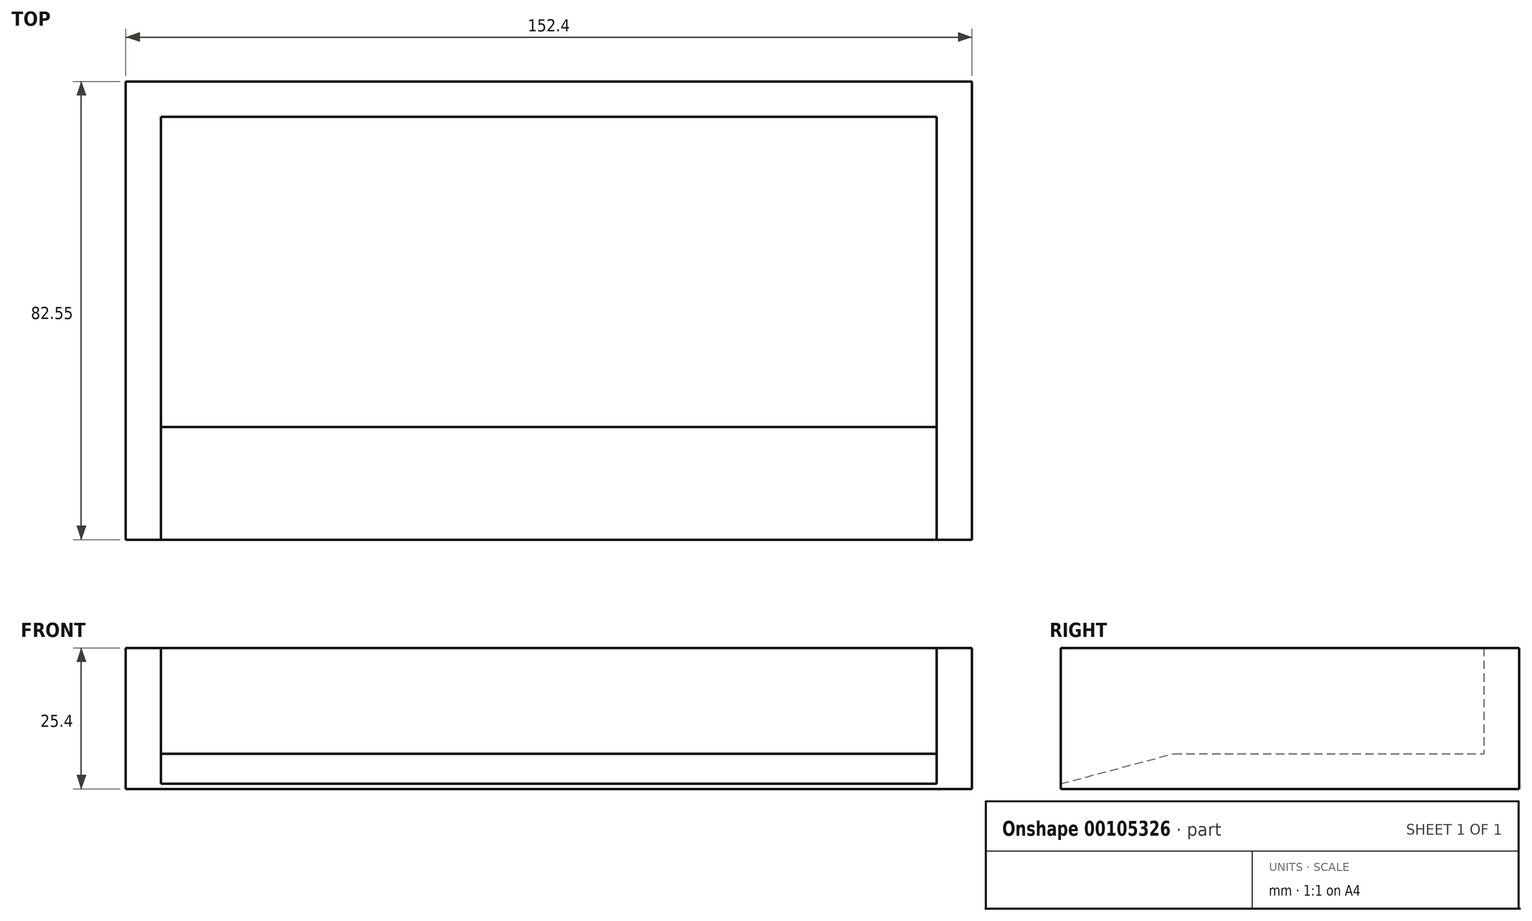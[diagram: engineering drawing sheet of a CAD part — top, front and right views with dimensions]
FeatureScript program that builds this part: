
annotation { "Feature Type Name" : "Feature", "Feature Type Description" : "" }
export const myFeature = defineFeature(function(context is Context, id is Id, definition is map)
    precondition{}
    {
        {
            var Q0;
            Q0=qCreatedBy(makeId("Front.planeOp"),FACE);
            var sketch = newSketch(context, id + "F0", { "sketchPlane" : qUnion([Q0])});
            skLineSegment(sketch, "E0.bottom", {"start": v(76.2, -12.7) * mm, "end": v(-76.2, -12.7) * mm});
            skLineSegment(sketch, "E0.left", {"start": v(76.2, -12.7) * mm, "end": v(76.2, 12.7) * mm});
            skLineSegment(sketch, "E0.right", {"start": v(-76.2, -12.7) * mm, "end": v(-76.2, 12.7) * mm});
            skPoint(sketch, "E0.middle", {"position": v(0, 0) * mm});
            skLineSegment(sketch, "E1", {"start": v(-76.2, -12.7) * mm, "end": v(-76.2, -6.35) * mm});
            skLineSegment(sketch, "E2", {"start": v(-76.2, 12.7) * mm, "end": v(-69.85, 12.7) * mm});
            skLineSegment(sketch, "E3", {"start": v(-69.85, 12.7) * mm, "end": v(-69.85, -6.35) * mm});
            skLineSegment(sketch, "E4", {"start": v(76.2, -12.7) * mm, "end": v(69.85, -12.7) * mm});
            skLineSegment(sketch, "E5", {"start": v(69.85, 12.7) * mm, "end": v(69.85, -6.35) * mm});
            skLineSegment(sketch, "E6", {"start": v(-69.85, -6.35) * mm, "end": v(69.85, -6.35) * mm});
            skLineSegment(sketch, "E7", {"start": v(69.85, 12.7) * mm, "end": v(76.2, 12.7) * mm});
            skSolve(sketch);
        }
        {
            var Q0;
            Q0 = qSketchRegion(id + "F0", true);
            extrude(context, id + "F1", {"entities" : qUnion([Q0]), "depth" : 76.2 * mm});
        }
        {
            var Q0;
            Q0=makeQuery(id+"F1.opExtrude","CAP_EDGE",EDGE,{"disambiguationData":[OSD([sQuery(id+"F0.wireOp",EDGE,"E6")])],"isStart":false});
            chamfer(context, id + "F2", {"entities" : qUnion([Q0]), "chamferType" : ChamferType.OFFSET_ANGLE, "width" : 20.32 * mm, "oppositeDirection" : false, "angle" : 15 * degree, "tangentPropagation" : true});
        }
        {
            var Q0;
            Q0=qCreatedBy(makeId("Front.planeOp"),FACE);
            var sketch = newSketch(context, id + "F3", { "sketchPlane" : qUnion([Q0])});
            skLineSegment(sketch, "E8.bottom", {"start": v(-76.2, 12.7) * mm, "end": v(76.2, 12.7) * mm});
            skLineSegment(sketch, "E8.top", {"start": v(-76.2, -12.7) * mm, "end": v(76.2, -12.7) * mm});
            skLineSegment(sketch, "E8.left", {"start": v(-76.2, 12.7) * mm, "end": v(-76.2, -12.7) * mm});
            skLineSegment(sketch, "E8.right", {"start": v(76.2, 12.7) * mm, "end": v(76.2, -12.7) * mm});
            skPoint(sketch, "E8.middle", {"position": v(0, 0) * mm});
            skSolve(sketch);
        }
        {
            var Q0;
            Q0 = qSketchRegion(id + "F3", true);
            extrude(context, id + "F4", {"entities" : qUnion([Q0]), "operationType" : NewBodyOperationType.ADD, "oppositeDirection" : true, "depth" : 6.35 * mm});
        }
    });
